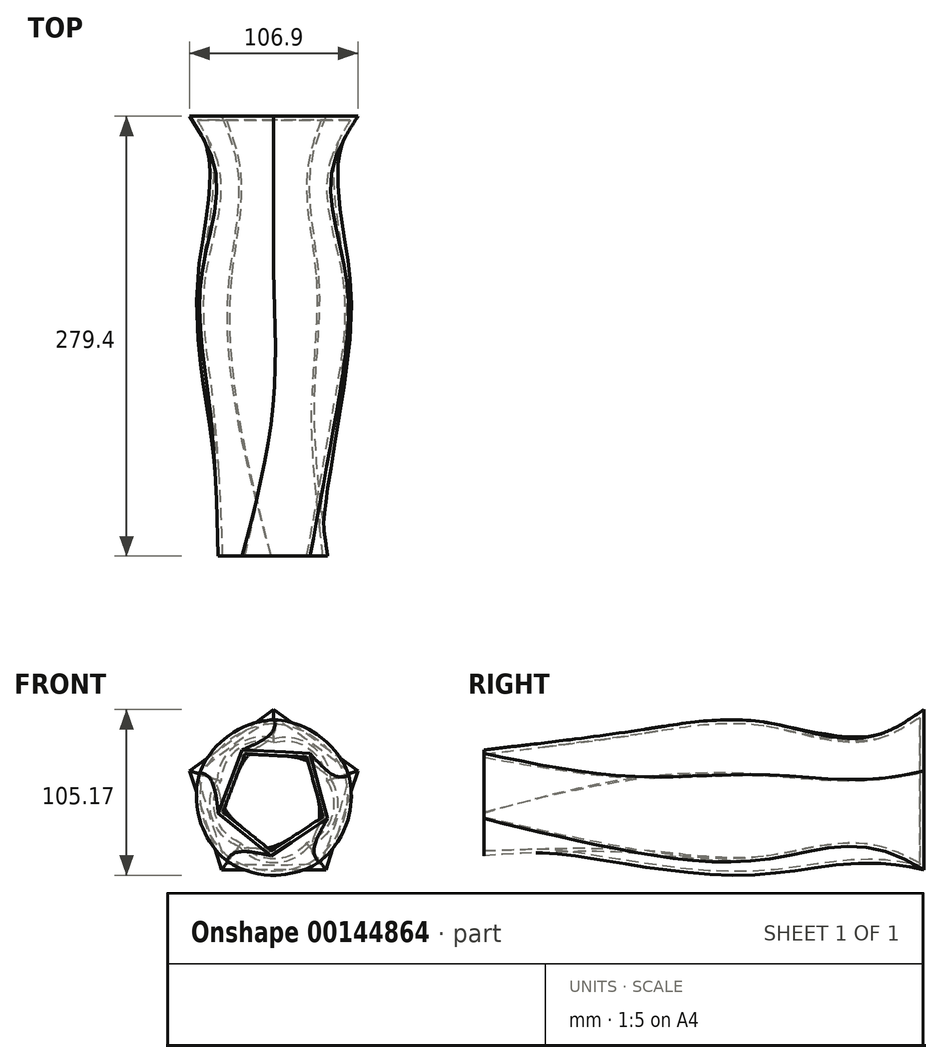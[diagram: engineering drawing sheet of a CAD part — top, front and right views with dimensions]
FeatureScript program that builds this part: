
annotation { "Feature Type Name" : "Feature", "Feature Type Description" : "" }
export const myFeature = defineFeature(function(context is Context, id is Id, definition is map)
    precondition{}
    {
        {
            var Q0;
            Q0=qCreatedBy(makeId("Front.planeOp"),FACE);
            cPlane(context, id + "F0", {"entities" : qUnion([Q0]), "cplaneType" : CPlaneType.OFFSET, "offset" : 25.4 * mm, "width" : 152.4 * mm, "height" : 152.4 * mm});
        }
        {
            var Q0;
            Q0=qCreatedBy(id+"F0.planeOp",FACE);
            cPlane(context, id + "F1", {"entities" : qUnion([Q0]), "cplaneType" : CPlaneType.OFFSET, "offset" : 25.4 * mm, "width" : 152.4 * mm, "height" : 152.4 * mm});
        }
        {
            var Q0;
            Q0=qCreatedBy(id+"F1.planeOp",FACE);
            cPlane(context, id + "F2", {"entities" : qUnion([Q0]), "cplaneType" : CPlaneType.OFFSET, "offset" : 76.2 * mm, "width" : 152.4 * mm, "height" : 152.4 * mm});
        }
        {
            var Q0;
            Q0=qCreatedBy(id+"F2.planeOp",FACE);
            cPlane(context, id + "F3", {"entities" : qUnion([Q0]), "cplaneType" : CPlaneType.OFFSET, "offset" : 76.2 * mm, "width" : 152.4 * mm, "height" : 152.4 * mm});
        }
        {
            var Q0;
            Q0=qCreatedBy(id+"F3.planeOp",FACE);
            cPlane(context, id + "F4", {"entities" : qUnion([Q0]), "cplaneType" : CPlaneType.OFFSET, "offset" : 101.6 * mm, "width" : 152.4 * mm, "height" : 152.4 * mm});
        }
        {
            var Q0;
            Q0=qCreatedBy(id+"F0.planeOp",FACE);
            var sketch = newSketch(context, id + "F5", { "sketchPlane" : qUnion([Q0])});
            skCircle(sketch, "E0.cCircle", {"center": v(0, 0) * mm, "radius": 45.46 * mm, "construction": true});
            skLineSegment(sketch, "E0.0", {"start": v(-53.45, 17.37) * mm, "end": v(0, 56.2) * mm});
            skLineSegment(sketch, "E0.1", {"start": v(0, 56.2) * mm, "end": v(53.45, 17.37) * mm});
            skLineSegment(sketch, "E0.2", {"start": v(53.45, 17.37) * mm, "end": v(33.03, -45.46) * mm});
            skLineSegment(sketch, "E0.3", {"start": v(33.03, -45.46) * mm, "end": v(-33.03, -45.46) * mm});
            skLineSegment(sketch, "E0.4", {"start": v(-33.03, -45.46) * mm, "end": v(-53.45, 17.37) * mm});
            skPoint(sketch, "E0.0.midPoint", {"position": v(-26.72, 36.78) * mm});
            skSolve(sketch);
        }
        {
            var Q0;
            Q0=qCreatedBy(id+"F1.planeOp",FACE);
            var sketch = newSketch(context, id + "F6", { "sketchPlane" : qUnion([Q0])});
            skCircle(sketch, "E1", {"center": v(0, 0) * mm, "radius": 41.49 * mm});
            skSolve(sketch);
        }
        {
            var Q0;
            Q0=qCreatedBy(id+"F2.planeOp",FACE);
            var sketch = newSketch(context, id + "F7", { "sketchPlane" : qUnion([Q0])});
            skCircle(sketch, "E2", {"center": v(0, 0) * mm, "radius": 48.33 * mm});
            skSolve(sketch);
        }
        {
            var Q0;
            Q0=qCreatedBy(id+"F3.planeOp",FACE);
            var sketch = newSketch(context, id + "F8", { "sketchPlane" : qUnion([Q0])});
            skCircle(sketch, "E3", {"center": v(0, 0) * mm, "radius": 43.64 * mm});
            skSolve(sketch);
        }
        {
            var Q0;
            Q0=qCreatedBy(id+"F4.planeOp",FACE);
            var sketch = newSketch(context, id + "F9", { "sketchPlane" : qUnion([Q0])});
            skCircle(sketch, "E4.cCircle", {"center": v(0, 0) * mm, "radius": 29.62 * mm, "construction": true});
            skLineSegment(sketch, "E4.0", {"start": v(-35.33, -9.6) * mm, "end": v(-20.04, 30.64) * mm});
            skLineSegment(sketch, "E4.1", {"start": v(-20.04, 30.64) * mm, "end": v(22.95, 28.53) * mm});
            skLineSegment(sketch, "E4.2", {"start": v(22.95, 28.53) * mm, "end": v(34.22, -13) * mm});
            skLineSegment(sketch, "E4.3", {"start": v(34.22, -13) * mm, "end": v(-1.8, -36.57) * mm});
            skLineSegment(sketch, "E4.4", {"start": v(-1.8, -36.57) * mm, "end": v(-35.33, -9.6) * mm});
            skPoint(sketch, "E4.0.midPoint", {"position": v(-27.69, 10.52) * mm});
            skSolve(sketch);
        }
        {
            var Q0;
            Q0=makeQuery(id+"F5.imprint","IMPRINT",FACE,{"disambiguationData":[TD([[makeQuery(id+"F5.imprint","IMPRINT",EDGE,{"derivedFrom":sQuery(id+"F5.wireOp",EDGE,"E0.0")}),-1.0]])]});
            var Q1;
            Q1=makeQuery(id+"F6.imprint","IMPRINT",FACE,{"disambiguationData":[TD([[makeQuery(id+"F6.imprint","IMPRINT",EDGE,{"derivedFrom":sQuery(id+"F6.wireOp",EDGE,"E1")}),1.0]])]});
            var Q2;
            Q2=makeQuery(id+"F7.imprint","IMPRINT",FACE,{"disambiguationData":[TD([[makeQuery(id+"F7.imprint","IMPRINT",EDGE,{"derivedFrom":sQuery(id+"F7.wireOp",EDGE,"E2")}),1.0]])]});
            var Q3;
            Q3=makeQuery(id+"F8.imprint","IMPRINT",FACE,{"disambiguationData":[TD([[makeQuery(id+"F8.imprint","IMPRINT",EDGE,{"derivedFrom":sQuery(id+"F8.wireOp",EDGE,"E3")}),1.0]])]});
            var Q4;
            Q4=makeQuery(id+"F9.imprint","IMPRINT",FACE,{"disambiguationData":[TD([[makeQuery(id+"F9.imprint","IMPRINT",EDGE,{"derivedFrom":sQuery(id+"F9.wireOp",EDGE,"E4.0")}),-1.0]])]});
            loft(context, id + "F10", {"sheetProfilesArray" : [{ "sheetProfileEntities" : qUnion([Q0]) }, { "sheetProfileEntities" : qUnion([Q1]) }, { "sheetProfileEntities" : qUnion([Q2]) }, { "sheetProfileEntities" : qUnion([Q3]) }, { "sheetProfileEntities" : qUnion([Q4]) }]});
        }
        {
            var Q0;
            Q0=makeQuery(id+"F10.opLoft","CAP_FACE",FACE,{"disambiguationData":[OSD([makeQuery(id+"F9.imprint","IMPRINT",FACE,{"disambiguationData":[TD([[makeQuery(id+"F9.imprint","IMPRINT",EDGE,{"derivedFrom":sQuery(id+"F9.wireOp",EDGE,"E4.0")}),-1.0]])]})])],"isStart":true});
            shell(context, id + "F11", {"entities" : qUnion([Q0]), "thickness" : 2.54 * mm});
        }
    });
